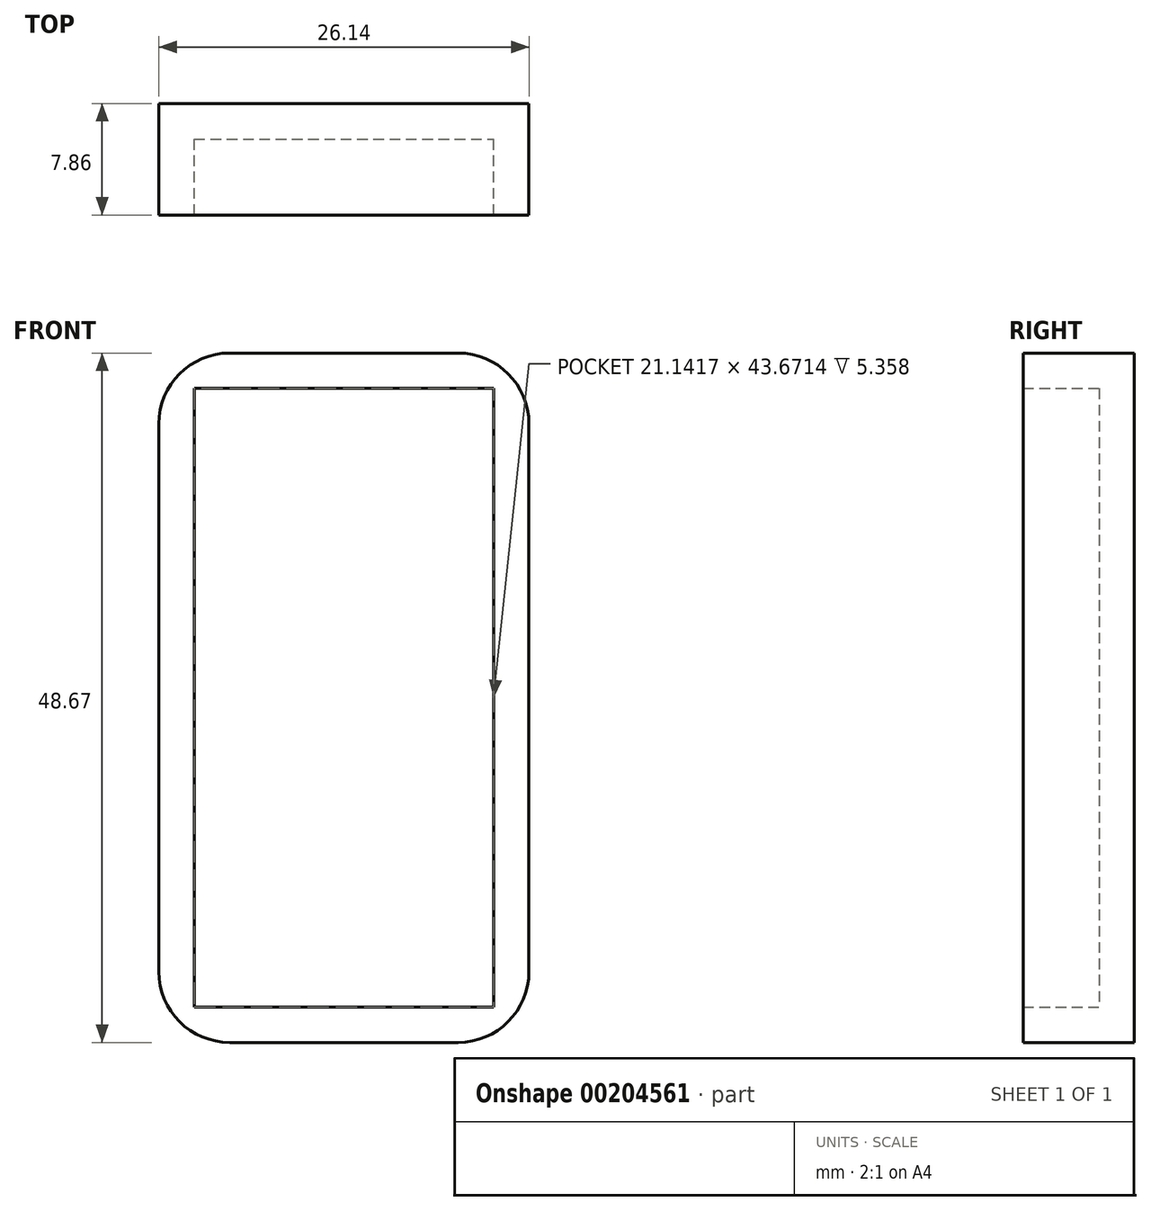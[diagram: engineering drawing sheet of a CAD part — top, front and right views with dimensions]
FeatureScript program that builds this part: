
annotation { "Feature Type Name" : "Feature", "Feature Type Description" : "" }
export const myFeature = defineFeature(function(context is Context, id is Id, definition is map)
    precondition{}
    {
        {
            var Q0;
            Q0=qCreatedBy(makeId("Front.planeOp"),FACE);
            var sketch = newSketch(context, id + "F0", { "sketchPlane" : qUnion([Q0])});
            skLineSegment(sketch, "E0.bottom", {"start": v(-12.75, 17.08) * mm, "end": v(13.39, 17.08) * mm});
            skLineSegment(sketch, "E0.top", {"start": v(-12.75, -31.59) * mm, "end": v(13.39, -31.59) * mm});
            skLineSegment(sketch, "E0.left", {"start": v(-12.75, 17.08) * mm, "end": v(-12.75, -31.59) * mm});
            skLineSegment(sketch, "E0.right", {"start": v(13.39, 17.08) * mm, "end": v(13.39, -31.59) * mm});
            skSolve(sketch);
        }
        {
            var Q0;
            Q0 = qSketchRegion(id + "F0", true);
            extrude(context, id + "F1", {"entities" : qUnion([Q0]), "depth" : 7.86 * mm});
        }
        {
            var Q0;
            Q0=makeQuery(id+"F1.opExtrude","CAP_FACE",FACE,{"disambiguationData":[OSD([sQuery(id+"F0.wireOp",EDGE,"E0.bottom"),sQuery(id+"F0.wireOp",EDGE,"E0.top"),sQuery(id+"F0.wireOp",EDGE,"E0.left"),sQuery(id+"F0.wireOp",EDGE,"E0.right")])],"isStart":false});
            shell(context, id + "F2", {"entities" : qUnion([Q0]), "thickness" : 2.5 * mm});
        }
        {
            var Q0;
            Q0=makeQuery(id+"F1.opExtrude","SWEPT_EDGE",EDGE,{"disambiguationData":[OSD([sQuery(id+"F0.wireOp",EDGE,"E0.bottom"),sQuery(id+"F0.wireOp",EDGE,"E0.right")])]});
            var Q1;
            Q1=makeQuery(id+"F1.opExtrude","SWEPT_EDGE",EDGE,{"disambiguationData":[OSD([sQuery(id+"F0.wireOp",EDGE,"E0.bottom"),sQuery(id+"F0.wireOp",EDGE,"E0.left")])]});
            var Q2;
            Q2=makeQuery(id+"F1.opExtrude","SWEPT_EDGE",EDGE,{"disambiguationData":[OSD([sQuery(id+"F0.wireOp",EDGE,"E0.top"),sQuery(id+"F0.wireOp",EDGE,"E0.left")])]});
            var Q3;
            Q3=makeQuery(id+"F1.opExtrude","SWEPT_EDGE",EDGE,{"disambiguationData":[OSD([sQuery(id+"F0.wireOp",EDGE,"E0.top"),sQuery(id+"F0.wireOp",EDGE,"E0.right")])]});
            fillet(context, id + "F3", {"entities" : qUnion([Q0, Q1, Q2, Q3]), "radius" : 5 * mm, "tangentPropagation" : true, "allowEdgeOverflow" : false});
        }
    });
